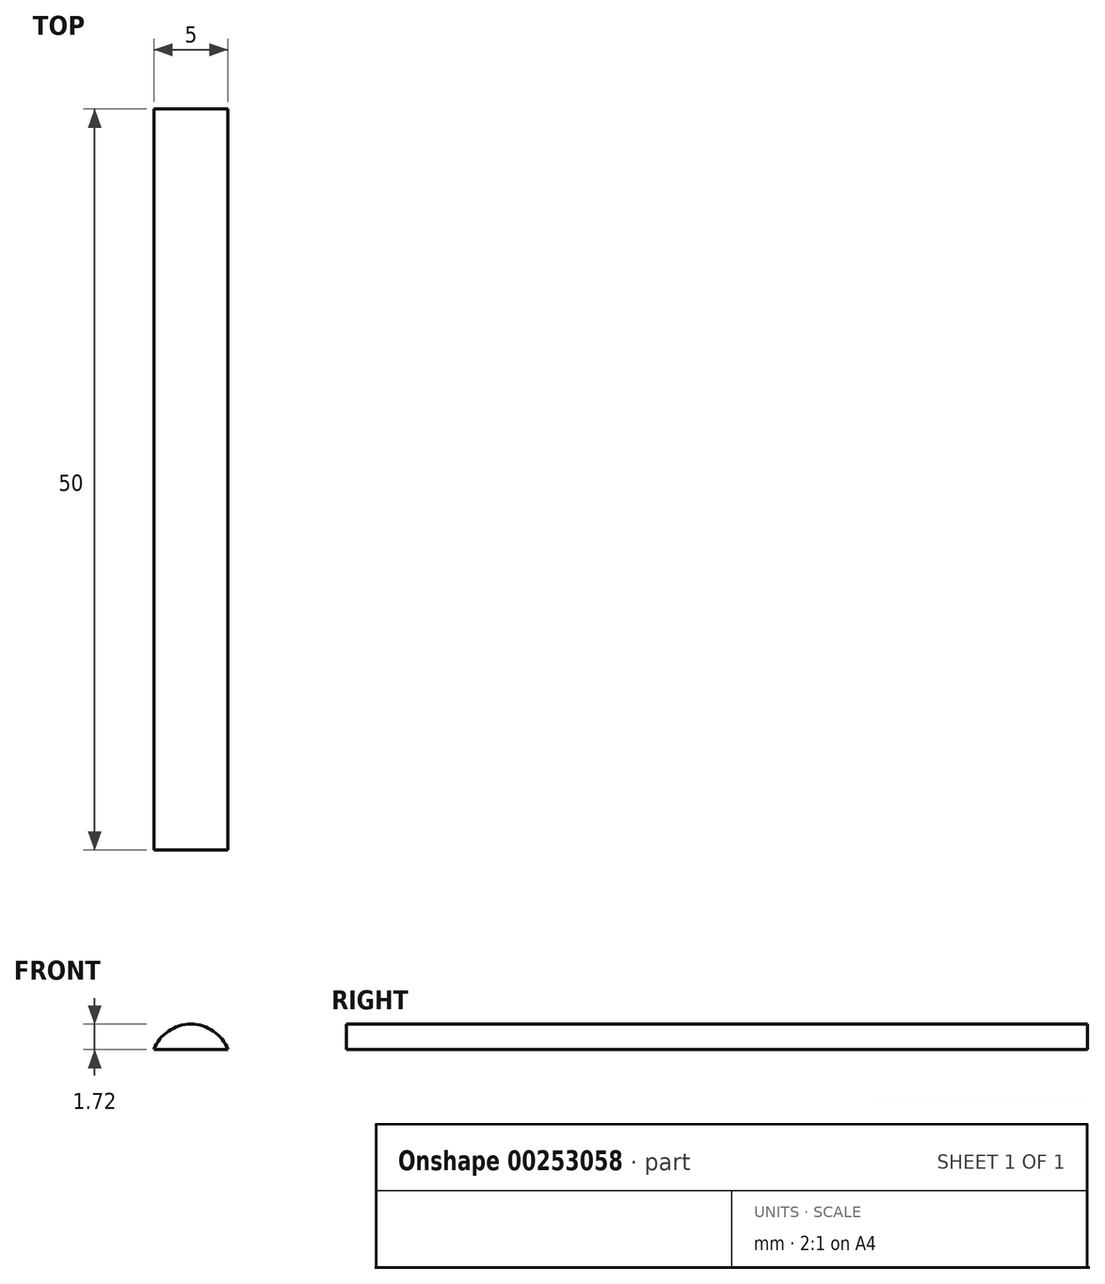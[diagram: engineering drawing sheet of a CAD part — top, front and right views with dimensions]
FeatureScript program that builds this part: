
annotation { "Feature Type Name" : "Feature", "Feature Type Description" : "" }
export const myFeature = defineFeature(function(context is Context, id is Id, definition is map)
    precondition{}
    {
        {
            var Q0;
            Q0=qCreatedBy(makeId("Front.planeOp"),FACE);
            var sketch = newSketch(context, id + "F0", { "sketchPlane" : qUnion([Q0])});
            skLineSegment(sketch, "E0", {"start": v(-24.51, 0) * mm, "end": v(-19.51, 0) * mm});
            skLineSegment(sketch, "E1", {"start": v(-22.01, 0) * mm, "end": v(-22.01, 2.8) * mm, "construction": true});
            skArc(sketch, "E2", {"start": v(-19.51, 0) * mm, "mid": v(-22.01, 1.72) * mm, "end": v(-24.51, 0) * mm});
            skSolve(sketch);
        }
        {
            var Q0;
            Q0=makeQuery(id+"F0.imprint","IMPRINT",FACE,{"disambiguationData":[TD([[makeQuery(id+"F0.imprint","IMPRINT",EDGE,{"derivedFrom":sQuery(id+"F0.wireOp",EDGE,"E0")}),1.0]])]});
            extrude(context, id + "F1", {"entities" : qUnion([Q0]), "depth" : 50 * mm});
        }
    });
